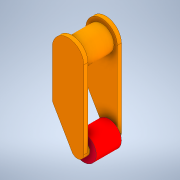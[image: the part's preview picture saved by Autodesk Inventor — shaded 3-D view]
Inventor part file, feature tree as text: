
AUTODESK INVENTOR PART (.ipt)
format: ipt  version: 2021 (Build 250183000, 183)  size: 177,664 bytes
history: native  units: mm
features: extrude x5, sketch x5, fillet x2, mirror x1
ambient origin geometry x8: Origin, YZ Plane, XZ Plane, XY Plane, X Axis, Y Axis, Z Axis, Center Point
bodies: Solid1 (feature_tree), Solid2 (feature_tree)
feature tree (13):
  extrude  "Extrusion1"  Depth=12.0mm TaperAngle=0.0deg
  extrude  "Extrusion2"  TaperAngle=0.0deg  [1 undecoded]
  extrude  "Extrusion3"  Depth=15.0mm
  extrude  "Extrusion4"  TaperAngle=150.0deg  [1 undecoded]
  extrude  "Extrusion5"  Depth=12.0mm
  fillet  "Fillet1"  Radius=8.0mm
  fillet  "Fillet2"  Radius=7.5mm
  mirror  "Mirror1"
  sketch  "Sketch1"  dims[d0=12.0mm d1=12.0mm d2=0.0mm]
  sketch  "Sketch2"  dims[d3=6.0mm d4=0.0mm d5=0.0mm]
  sketch  "Sketch3"  dims[d6=2.0mm d7=0.0mm d11=15.0mm]
  sketch  "Sketch5"  dims[d12=30.0mm d13=150.0deg]
  sketch  "Sketch6"  dims[d14=2.0mm d15=0.0mm d16=12.0mm d17=8.0mm d18=7.5mm d19=18.0mm d20=0.0mm d21=2.0mm]
note: 2 required parameter values undecoded (feature->parameter linkage not recoverable at this tier; creation-order binding heuristic only, values carry confidence <= 0.55)
